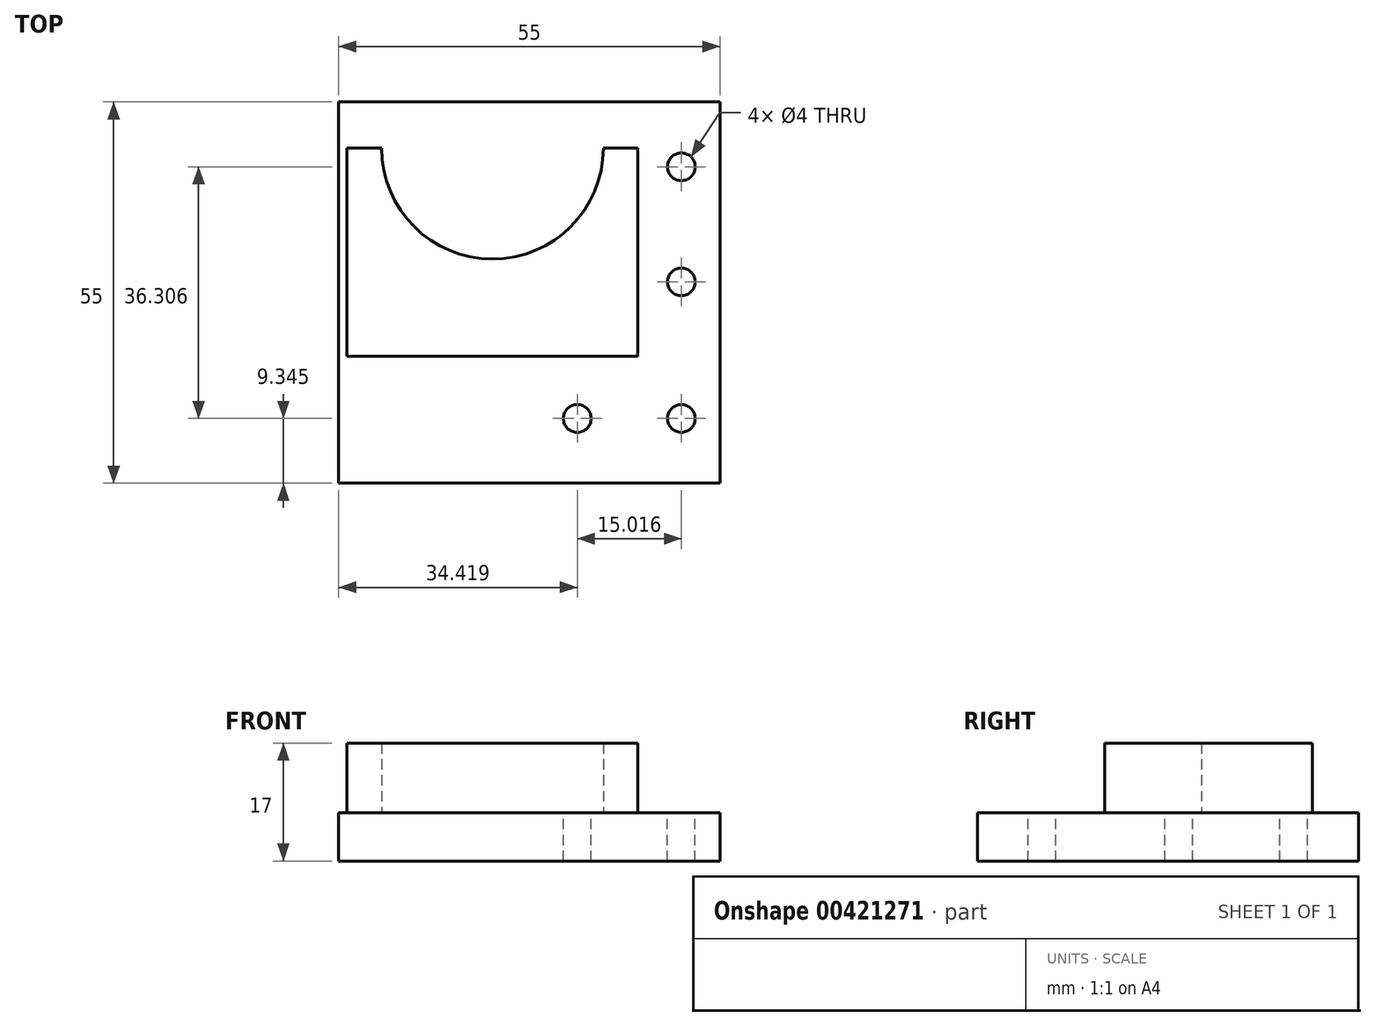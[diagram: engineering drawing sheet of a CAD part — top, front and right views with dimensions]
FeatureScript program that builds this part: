
annotation { "Feature Type Name" : "Feature", "Feature Type Description" : "" }
export const myFeature = defineFeature(function(context is Context, id is Id, definition is map)
    precondition{}
    {
        {
            var Q0;
            Q0=qCreatedBy(makeId("Top.planeOp"),FACE);
            var sketch = newSketch(context, id + "F0", { "sketchPlane" : qUnion([Q0])});
            skLineSegment(sketch, "E0.bottom", {"start": v(0, 0) * mm, "end": v(-55, 0) * mm});
            skLineSegment(sketch, "E0.top", {"start": v(0, 55) * mm, "end": v(-55, 55) * mm});
            skLineSegment(sketch, "E0.left", {"start": v(0, 0) * mm, "end": v(0, 55) * mm});
            skLineSegment(sketch, "E0.right", {"start": v(-55, 0) * mm, "end": v(-55, 55) * mm});
            skSolve(sketch);
        }
        {
            var Q0;
            Q0=qSketchRegion(id+"F0",true);
            extrude(context, id + "F1", {"entities" : qUnion([Q0]), "depth" : 7 * mm});
        }
        {
            var Q0;
            Q0=makeQuery(id+"F1.opExtrude","CAP_FACE",FACE,{"disambiguationData":[OSD([sQuery(id+"F0.wireOp",EDGE,"E0.bottom"),sQuery(id+"F0.wireOp",EDGE,"E0.top"),sQuery(id+"F0.wireOp",EDGE,"E0.left"),sQuery(id+"F0.wireOp",EDGE,"E0.right")])],"isStart":false});
            var sketch = newSketch(context, id + "F2", { "sketchPlane" : qUnion([Q0])});
            skArc(sketch, "E1", {"start": v(-38.18, 48.34) * mm, "mid": v(-22.18, 32.34) * mm, "end": v(-6.18, 48.34) * mm});
            skLineSegment(sketch, "E2", {"start": v(-38.18, 48.34) * mm, "end": v(-43.18, 48.34) * mm});
            skLineSegment(sketch, "E3", {"start": v(-43.18, 48.34) * mm, "end": v(-43.18, 18.34) * mm});
            skLineSegment(sketch, "E4", {"start": v(-43.18, 18.34) * mm, "end": v(-1.18, 18.34) * mm});
            skLineSegment(sketch, "E5", {"start": v(-1.18, 18.34) * mm, "end": v(-1.18, 48.34) * mm});
            skLineSegment(sketch, "E6", {"start": v(-1.18, 48.34) * mm, "end": v(-6.18, 48.34) * mm});
            skLineSegment(sketch, "E7", {"start": v(-27.5, 55) * mm, "end": v(-27.5, 14.22) * mm});
            skLineSegment(sketch, "E8.MirrorCS", {"start": v(-16.82, 48.34) * mm, "end": v(-11.82, 48.34) * mm});
            skLineSegment(sketch, "E9.MirrorCS", {"start": v(-11.82, 48.34) * mm, "end": v(-11.82, 18.34) * mm});
            skLineSegment(sketch, "E10.MirrorCS", {"start": v(-53.82, 18.34) * mm, "end": v(-53.82, 48.34) * mm});
            skLineSegment(sketch, "E11.MirrorCS", {"start": v(-11.82, 18.34) * mm, "end": v(-53.82, 18.34) * mm});
            skLineSegment(sketch, "E12.MirrorCS", {"start": v(-53.82, 48.34) * mm, "end": v(-48.82, 48.34) * mm});
            skArc(sketch, "E13.MirrorCS", {"start": v(-16.82, 48.34) * mm, "mid": v(-32.82, 32.34) * mm, "end": v(-48.82, 48.34) * mm});
            skSolve(sketch);
        }
        {
            var Q0;
            Q0=makeQuery(id+"F1.opExtrude","CAP_FACE",FACE,{"disambiguationData":[OSD([sQuery(id+"F0.wireOp",EDGE,"E0.bottom"),sQuery(id+"F0.wireOp",EDGE,"E0.top"),sQuery(id+"F0.wireOp",EDGE,"E0.left"),sQuery(id+"F0.wireOp",EDGE,"E0.right")])],"isStart":false});
            var sketch = newSketch(context, id + "F3", { "sketchPlane" : qUnion([Q0])});
            skLineSegment(sketch, "E14", {"start": v(-27.5, 55) * mm, "end": v(-27.5, 0) * mm});
            skCircle(sketch, "E15.MirrorC", {"center": v(-20.58, 9.34) * mm, "radius": 2 * mm});
            skCircle(sketch, "E16.MirrorC", {"center": v(-5.57, 9.34) * mm, "radius": 2 * mm});
            skCircle(sketch, "E17.MirrorC", {"center": v(-5.57, 29.04) * mm, "radius": 2 * mm});
            skCircle(sketch, "E18.MirrorC", {"center": v(-5.57, 45.65) * mm, "radius": 2 * mm});
            skSolve(sketch);
        }
        {
            var Q0;
            {var subQ4=sQuery(id+"F2.wireOp",EDGE,"E10.MirrorCS");Q0=makeQuery(id+"F2.imprint","IMPRINT",FACE,{"disambiguationData":[TD([[makeQuery(id+"F2.imprint","IMPRINT",EDGE,{"derivedFrom":subQ4}),-1.0]])]});}
            var Q1;
            {var subQ0=sQuery(id+"F2.wireOp",EDGE,"E11.MirrorCS");var subQ1=sQuery(id+"F2.wireOp",EDGE,"E3");var subQ2=makeQuery(id+"F2.imprint","INTERSECT",VERTEX,{"derivedFrom":[subQ1,subQ0]});Q1=makeQuery(id+"F2.imprint","IMPRINT",FACE,{"disambiguationData":[TD([[makeQuery(id+"F2.imprint","IMPRINT",EDGE,{"disambiguationData":[TD([[subQ2,1.0]])],"derivedFrom":subQ1}),1.0]])]});}
            var Q2;
            {var subQ5=sQuery(id+"F2.wireOp",EDGE,"E8.MirrorCS");Q2=makeQuery(id+"F2.imprint","IMPRINT",FACE,{"disambiguationData":[TD([[makeQuery(id+"F2.imprint","IMPRINT",EDGE,{"derivedFrom":subQ5}),-1.0]])]});}
            var Q3;
            {var subQ0=sQuery(id+"F2.wireOp",EDGE,"E9.MirrorCS");var subQ1=sQuery(id+"F2.wireOp",EDGE,"E1");var subQ2=makeQuery(id+"F2.imprint","INTERSECT",VERTEX,{"derivedFrom":[subQ1,subQ0]});Q3=makeQuery(id+"F2.imprint","IMPRINT",FACE,{"disambiguationData":[TD([[makeQuery(id+"F2.imprint","IMPRINT",EDGE,{"disambiguationData":[TD([[subQ2,1.0]])],"derivedFrom":subQ1}),-1.0]])]});}
            extrude(context, id + "F4", {"entities" : qUnion([Q0, Q1, Q2, Q3]), "operationType" : NewBodyOperationType.ADD, "depth" : 10 * mm});
        }
        {
            var Q0;
            Q0=qSketchRegion(id+"F3",true);
            extrude(context, id + "F5", {"entities" : qUnion([Q0]), "operationType" : NewBodyOperationType.REMOVE, "endBound" : BoundingType.THROUGH_ALL, "oppositeDirection" : true, "depth" : 25 * mm});
        }
    });
